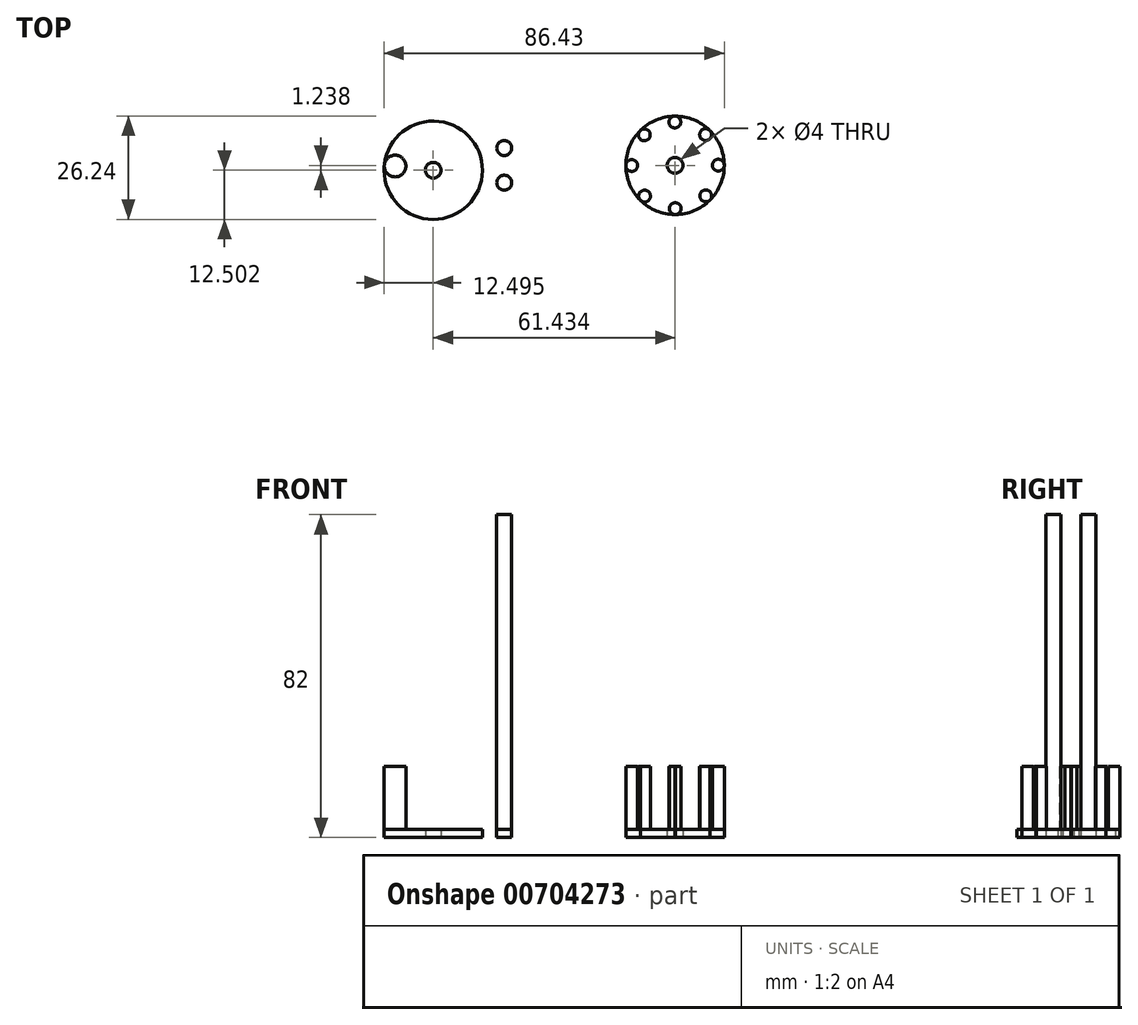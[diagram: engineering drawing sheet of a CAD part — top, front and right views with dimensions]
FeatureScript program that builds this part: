
annotation { "Feature Type Name" : "Feature", "Feature Type Description" : "" }
export const myFeature = defineFeature(function(context is Context, id is Id, definition is map)
    precondition{}
    {
        {
            var Q0;
            Q0=qCreatedBy(makeId("Top.planeOp"),FACE);
            var sketch = newSketch(context, id + "F0", { "sketchPlane" : qUnion([Q0])});
            skCircle(sketch, "E0", {"center": v(25.2, 0) * mm, "radius": 12.5 * mm});
            skCircle(sketch, "E1", {"center": v(25.2, 0) * mm, "radius": 2 * mm});
            skCircle(sketch, "E2", {"center": v(14.2, -0.05) * mm, "radius": 1.5 * mm});
            skPoint(sketch, "E2.first.point", {"position": v(12.7, 0) * mm});
            skPoint(sketch, "E2.second.point", {"position": v(15.7, 0) * mm});
            skPoint(sketch, "E2.third.point", {"position": v(15.5, 0.7) * mm});
            skPoint(sketch, "E3.center", {"position": v(26.5, -1.32) * mm});
            skCircle(sketch, "E4", {"center": v(-36.23, -1.24) * mm, "radius": 12.5 * mm});
            skPoint(sketch, "E4.first.point", {"position": v(-48.67, 0) * mm});
            skPoint(sketch, "E4.second.point", {"position": v(-23.8, 0) * mm});
            skPoint(sketch, "E4.third.point", {"position": v(-28.13, 8.28) * mm});
            skCircle(sketch, "E5", {"center": v(-45.93, -0.17) * mm, "radius": 2.75 * mm});
            skPoint(sketch, "E5.first.point", {"position": v(-43.18, -0.01) * mm});
            skPoint(sketch, "E5.third.point", {"position": v(-46.57, 2.5) * mm});
            skPoint(sketch, "E3.7.0.center.orphan", {"position": v(18.7, 8.28) * mm});
            skCircle(sketch, "E6.1.0", {"center": v(17.45, -7.81) * mm, "radius": 1.5 * mm});
            skCircle(sketch, "E6.2.0", {"center": v(25.25, -11) * mm, "radius": 1.5 * mm});
            skCircle(sketch, "E6.3.0", {"center": v(33.01, -7.75) * mm, "radius": 1.5 * mm});
            skCircle(sketch, "E6.4.0", {"center": v(36.2, 0.05) * mm, "radius": 1.5 * mm});
            skCircle(sketch, "E6.5.0", {"center": v(32.95, 7.81) * mm, "radius": 1.5 * mm});
            skCircle(sketch, "E6.6.0", {"center": v(25.15, 11) * mm, "radius": 1.5 * mm});
            skCircle(sketch, "E6.7.0", {"center": v(17.39, 7.75) * mm, "radius": 1.5 * mm});
            skCircle(sketch, "E7", {"center": v(-36.23, -1.24) * mm, "radius": 2 * mm});
            skCircle(sketch, "E8", {"center": v(-18.2, 4.4) * mm, "radius": 1.9 * mm});
            skCircle(sketch, "E9.MirrorC", {"center": v(-18.2, -4.4) * mm, "radius": 1.9 * mm});
            skSolve(sketch);
        }
        {
            var Q0;
            Q0 = qSketchRegion(id + "F0", true);
            extrude(context, id + "F1", {"entities" : qUnion([Q0]), "depth" : 2 * mm, "offsetDistance" : 25 * mm});
        }
        {
            var Q0;
            {var subQ0=sQuery(id+"F0.wireOp",EDGE,"E6.7.0");var subQ1=sQuery(id+"F0.wireOp",EDGE,"E0");var subQ2=makeQuery(id+"F0.imprint","INTERSECT",VERTEX,{"disambiguationData":[OD(0.0)],"derivedFrom":[subQ1,subQ0]});Q0=makeQuery(id+"F0.imprint","IMPRINT",FACE,{"disambiguationData":[TD([[makeQuery(id+"F0.imprint","IMPRINT",EDGE,{"disambiguationData":[TD([[subQ2,-1.0]])],"derivedFrom":subQ1}),1.0]])]});}
            var Q1;
            {var subQ0=sQuery(id+"F0.wireOp",EDGE,"E6.6.0");var subQ1=sQuery(id+"F0.wireOp",EDGE,"E0");var subQ2=makeQuery(id+"F0.imprint","INTERSECT",VERTEX,{"disambiguationData":[OD(0.0)],"derivedFrom":[subQ1,subQ0]});Q1=makeQuery(id+"F0.imprint","IMPRINT",FACE,{"disambiguationData":[TD([[makeQuery(id+"F0.imprint","IMPRINT",EDGE,{"disambiguationData":[TD([[subQ2,-1.0]])],"derivedFrom":subQ1}),1.0]])]});}
            var Q2;
            {var subQ0=sQuery(id+"F0.wireOp",EDGE,"E6.4.0");var subQ1=sQuery(id+"F0.wireOp",EDGE,"E0");var subQ2=makeQuery(id+"F0.imprint","INTERSECT",VERTEX,{"disambiguationData":[OD(0.0)],"derivedFrom":[subQ1,subQ0]});Q2=makeQuery(id+"F0.imprint","IMPRINT",FACE,{"disambiguationData":[TD([[makeQuery(id+"F0.imprint","IMPRINT",EDGE,{"disambiguationData":[TD([[subQ2,1.0]])],"derivedFrom":subQ1}),1.0]])]});}
            var Q3;
            {var subQ0=sQuery(id+"F0.wireOp",EDGE,"E6.5.0");var subQ1=sQuery(id+"F0.wireOp",EDGE,"E0");var subQ2=makeQuery(id+"F0.imprint","INTERSECT",VERTEX,{"disambiguationData":[OD(0.0)],"derivedFrom":[subQ1,subQ0]});Q3=makeQuery(id+"F0.imprint","IMPRINT",FACE,{"disambiguationData":[TD([[makeQuery(id+"F0.imprint","IMPRINT",EDGE,{"disambiguationData":[TD([[subQ2,-1.0]])],"derivedFrom":subQ1}),1.0]])]});}
            var Q4;
            {var subQ0=sQuery(id+"F0.wireOp",EDGE,"E6.3.0");var subQ1=sQuery(id+"F0.wireOp",EDGE,"E0");var subQ2=makeQuery(id+"F0.imprint","INTERSECT",VERTEX,{"disambiguationData":[OD(0.0)],"derivedFrom":[subQ1,subQ0]});Q4=makeQuery(id+"F0.imprint","IMPRINT",FACE,{"disambiguationData":[TD([[makeQuery(id+"F0.imprint","IMPRINT",EDGE,{"disambiguationData":[TD([[subQ2,-1.0]])],"derivedFrom":subQ1}),1.0]])]});}
            var Q5;
            {var subQ0=sQuery(id+"F0.wireOp",EDGE,"E6.2.0");var subQ1=sQuery(id+"F0.wireOp",EDGE,"E0");var subQ2=makeQuery(id+"F0.imprint","INTERSECT",VERTEX,{"disambiguationData":[OD(0.0)],"derivedFrom":[subQ1,subQ0]});Q5=makeQuery(id+"F0.imprint","IMPRINT",FACE,{"disambiguationData":[TD([[makeQuery(id+"F0.imprint","IMPRINT",EDGE,{"disambiguationData":[TD([[subQ2,-1.0]])],"derivedFrom":subQ1}),1.0]])]});}
            var Q6;
            {var subQ0=sQuery(id+"F0.wireOp",EDGE,"E6.1.0");var subQ1=sQuery(id+"F0.wireOp",EDGE,"E0");var subQ2=makeQuery(id+"F0.imprint","INTERSECT",VERTEX,{"disambiguationData":[OD(0.0)],"derivedFrom":[subQ1,subQ0]});Q6=makeQuery(id+"F0.imprint","IMPRINT",FACE,{"disambiguationData":[TD([[makeQuery(id+"F0.imprint","IMPRINT",EDGE,{"disambiguationData":[TD([[subQ2,-1.0]])],"derivedFrom":subQ1}),1.0]])]});}
            var Q7;
            {var subQ0=sQuery(id+"F0.wireOp",EDGE,"E2");var subQ1=sQuery(id+"F0.wireOp",EDGE,"E0");var subQ2=makeQuery(id+"F0.imprint","INTERSECT",VERTEX,{"disambiguationData":[OD(0.0)],"derivedFrom":[subQ1,subQ0]});Q7=makeQuery(id+"F0.imprint","IMPRINT",FACE,{"disambiguationData":[TD([[makeQuery(id+"F0.imprint","IMPRINT",EDGE,{"disambiguationData":[TD([[subQ2,-1.0]])],"derivedFrom":subQ1}),1.0]])]});}
            extrude(context, id + "F2", {"entities" : qUnion([Q0, Q1, Q2, Q3, Q4, Q5, Q6, Q7]), "operationType" : NewBodyOperationType.ADD, "depth" : 18 * mm, "offsetDistance" : 25 * mm});
        }
        {
            var Q0;
            {var subQ0=sQuery(id+"F0.wireOp",EDGE,"E5");var subQ1=sQuery(id+"F0.wireOp",EDGE,"E4");var subQ2=makeQuery(id+"F0.imprint","INTERSECT",VERTEX,{"disambiguationData":[OD(0.0)],"derivedFrom":[subQ1,subQ0]});Q0=makeQuery(id+"F0.imprint","IMPRINT",FACE,{"disambiguationData":[TD([[makeQuery(id+"F0.imprint","IMPRINT",EDGE,{"disambiguationData":[TD([[subQ2,1.0]])],"derivedFrom":subQ1}),1.0]])]});}
            extrude(context, id + "F3", {"entities" : qUnion([Q0]), "operationType" : NewBodyOperationType.ADD, "depth" : 18 * mm, "offsetDistance" : 25 * mm});
        }
        {
            var Q0;
            Q0=makeQuery(id+"F1.opExtrude","CAP_FACE",FACE,{"disambiguationData":[OSD([sQuery(id+"F0.wireOp",EDGE,"E9.MirrorC")])],"isStart":false});
            var Q1;
            Q1=makeQuery(id+"F1.opExtrude","CAP_FACE",FACE,{"disambiguationData":[OSD([sQuery(id+"F0.wireOp",EDGE,"E8")])],"isStart":false});
            extrude(context, id + "F4", {"entities" : qUnion([Q0, Q1]), "depth" : 80 * mm, "offsetDistance" : 25 * mm});
        }
    });
